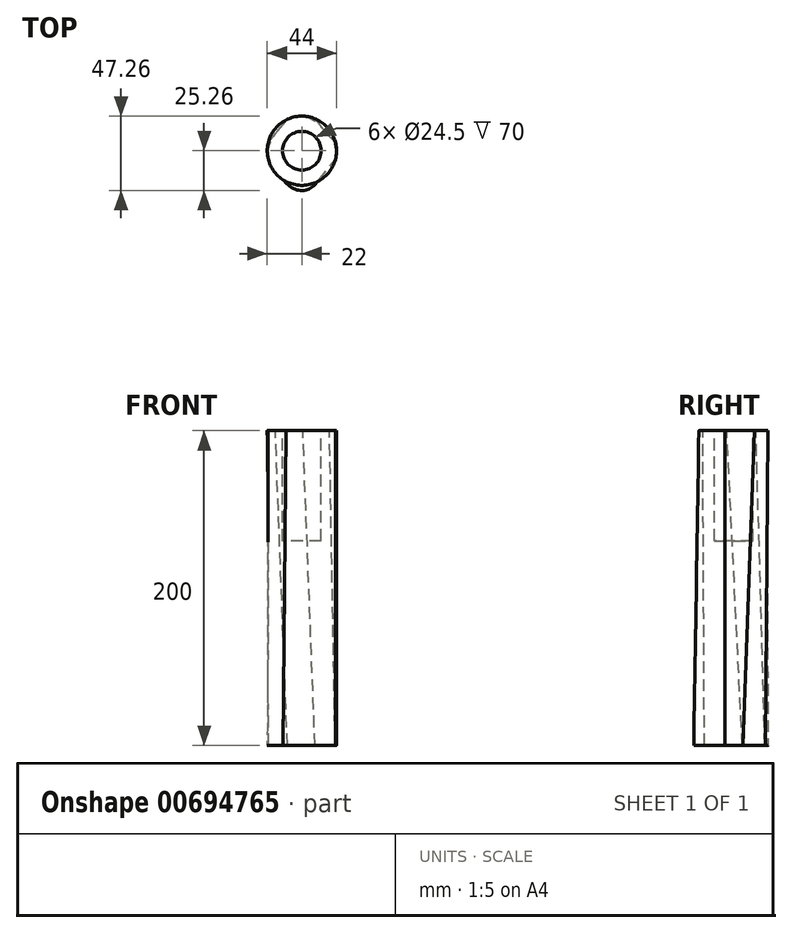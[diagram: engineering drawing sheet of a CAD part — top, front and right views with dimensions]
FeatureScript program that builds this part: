
annotation { "Feature Type Name" : "Feature", "Feature Type Description" : "" }
export const myFeature = defineFeature(function(context is Context, id is Id, definition is map)
    precondition{}
    {
        {
            var Q0;
            Q0=qCreatedBy(makeId("Top.planeOp"),FACE);
            var sketch = newSketch(context, id + "F0", { "sketchPlane" : qUnion([Q0])});
            skArc(sketch, "E0", {"start": v(21.3, -5.51) * mm, "mid": v(22, 0.29) * mm, "end": v(21.15, 6.07) * mm});
            skFitSpline(sketch, "E1", {"points": [v(-11.9, -18.5) * mm, v(-4, -24.59) * mm, v(4.72, -24.22) * mm, v(10.02, -19.59) * mm], "startDerivative": vector(18.22, -19.51) * mm, "endDerivative": vector(14.74, 17.56) * mm});
            skLineSegment(sketch, "E2", {"start": v(10.02, -19.59) * mm, "end": v(21.3, -5.51) * mm});
            skFitSpline(sketch, "E3", {"points": [v(21.15, 6.07) * mm, v(16.2, 10.2) * mm, v(8.32, 20.37) * mm], "startDerivative": vector(-11.88, 8.74) * mm, "endDerivative": vector(-16.68, 18.65) * mm});
            skArc(sketch, "E4.trimOffspring", {"start": v(8.32, 20.37) * mm, "mid": v(-0.5, 22) * mm, "end": v(-9.23, 19.97) * mm});
            skLineSegment(sketch, "E5", {"start": v(-21.28, 5.59) * mm, "end": v(-9.23, 19.97) * mm});
            skArc(sketch, "E6.trimOffspring", {"start": v(-21.28, 5.59) * mm, "mid": v(-20.5, -7.99) * mm, "end": v(-11.9, -18.5) * mm});
            skSolve(sketch);
        }
        {
            var Q0;
            Q0=qCreatedBy(makeId("Top.planeOp"),FACE);
            cPlane(context, id + "F1", {"entities" : qUnion([Q0]), "cplaneType" : CPlaneType.OFFSET, "offset" : 200 * mm, "width" : 150 * mm, "height" : 150 * mm});
        }
        {
            var Q0;
            Q0=qCreatedBy(id+"F1.planeOp",FACE);
            var sketch = newSketch(context, id + "F2", { "sketchPlane" : qUnion([Q0])});
            skCircle(sketch, "E7", {"center": v(0, 0) * mm, "radius": 22 * mm});
            skSolve(sketch);
        }
        {
            var Q0;
            Q0=makeQuery(id+"F0.imprint","IMPRINT",FACE,{"disambiguationData":[TD([[makeQuery(id+"F0.imprint","IMPRINT",EDGE,{"derivedFrom":sQuery(id+"F0.wireOp",EDGE,"E0")}),1.0]])]});
            var Q1;
            Q1=makeQuery(id+"F2.imprint","IMPRINT",FACE,{"disambiguationData":[TD([[makeQuery(id+"F2.imprint","IMPRINT",EDGE,{"derivedFrom":sQuery(id+"F2.wireOp",EDGE,"E7")}),1.0]])]});
            loft(context, id + "F3", {"sheetProfilesArray" : [{ "sheetProfileEntities" : qUnion([Q0]) }, { "sheetProfileEntities" : qUnion([Q1]) }]});
        }
        {
            var Q0;
            Q0=makeQuery(id+"F3.opLoft","CAP_FACE",FACE,{"disambiguationData":[OSD([makeQuery(id+"F2.imprint","IMPRINT",FACE,{"disambiguationData":[TD([[makeQuery(id+"F2.imprint","IMPRINT",EDGE,{"derivedFrom":sQuery(id+"F2.wireOp",EDGE,"E7")}),1.0]])]})])],"isStart":true});
            var sketch = newSketch(context, id + "F4", { "sketchPlane" : qUnion([Q0])});
            skCircle(sketch, "E8", {"center": v(0, 0) * mm, "radius": 12.25 * mm});
            skSolve(sketch);
        }
        {
            var Q0;
            Q0 = qSketchRegion(id + "F4", true);
            extrude(context, id + "F5", {"entities" : qUnion([Q0]), "operationType" : NewBodyOperationType.REMOVE, "oppositeDirection" : true, "depth" : 70 * mm, "offsetDistance" : 25 * mm});
        }
    });
